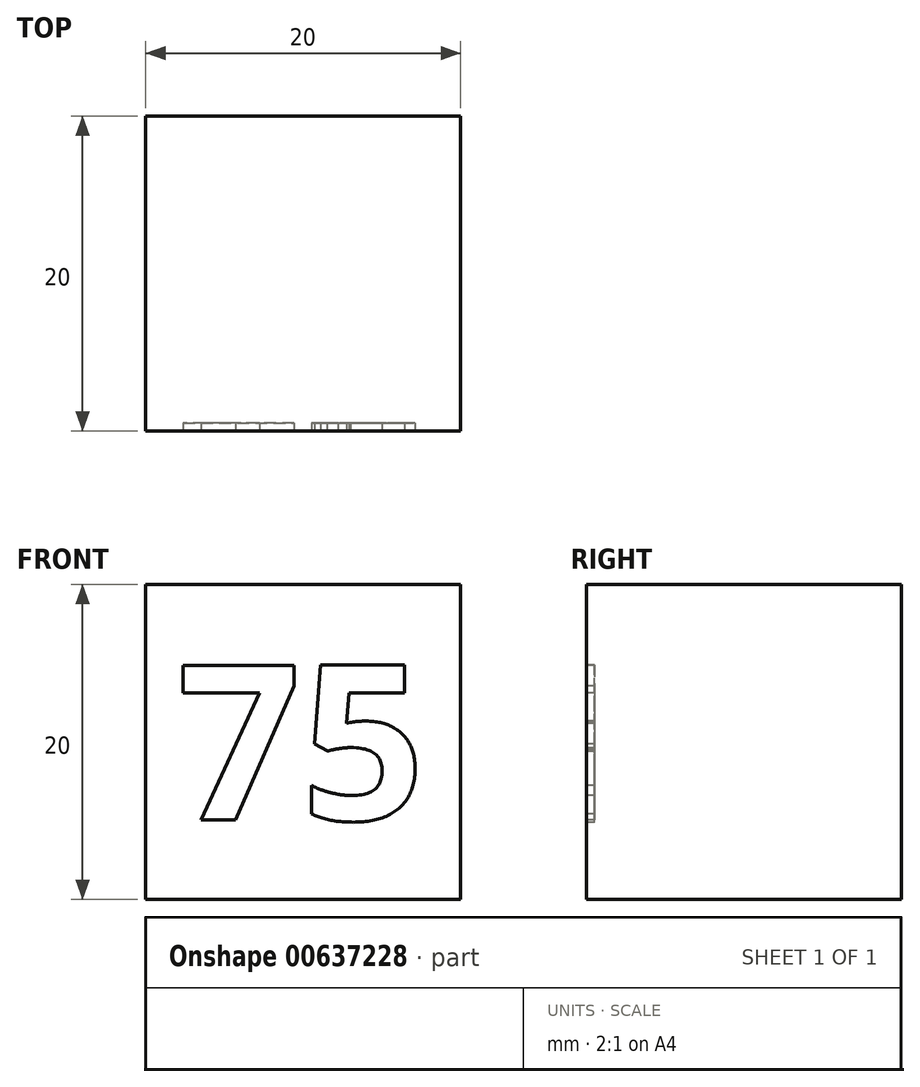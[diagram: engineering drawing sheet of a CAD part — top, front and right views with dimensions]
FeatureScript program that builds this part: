
annotation { "Feature Type Name" : "Feature", "Feature Type Description" : "" }
export const myFeature = defineFeature(function(context is Context, id is Id, definition is map)
    precondition{}
    {
        {
            var Q0;
            Q0=qCreatedBy(makeId("Top.planeOp"),FACE);
            var sketch = newSketch(context, id + "F0", { "sketchPlane" : qUnion([Q0])});
            skLineSegment(sketch, "E0.bottom", {"start": v(10, -10) * mm, "end": v(-10, -10) * mm});
            skLineSegment(sketch, "E0.top", {"start": v(10, 10) * mm, "end": v(-10, 10) * mm});
            skLineSegment(sketch, "E0.left", {"start": v(10, -10) * mm, "end": v(10, 10) * mm});
            skLineSegment(sketch, "E0.right", {"start": v(-10, -10) * mm, "end": v(-10, 10) * mm});
            skPoint(sketch, "E0.middle", {"position": v(0, 0) * mm});
            skSolve(sketch);
        }
        {
            var Q0;
            Q0 = qSketchRegion(id + "F0", true);
            extrude(context, id + "F1", {"entities" : qUnion([Q0]), "endBound" : BoundingType.SYMMETRIC, "depth" : 20 * mm, "offsetDistance" : 25 * mm});
        }
        {
            var Q0;
            Q0=makeQuery(id+"F1.opExtrude","SWEPT_FACE",FACE,{"disambiguationData":[OSD([sQuery(id+"F0.wireOp",EDGE,"E0.bottom")])]});
            var sketch = newSketch(context, id + "F2", { "sketchPlane" : qUnion([Q0])});
            skText(sketch, "E1", { "text": "75", "fontName": "OpenSans-Bold.ttf"});
            skLineSegment(sketch, "E2", {"start": v(-8, 0) * mm, "end": v(8, 0) * mm, "construction": true});
            const initialGuessF2  = {"E1": [-0.008, -0.00496, 1, 0, 0.00992]};
            skSetInitialGuess(sketch, initialGuessF2);
            skSolve(sketch);
        }
        {
            var Q0;
            Q0 = qSketchRegion(id + "F2", true);
            extrude(context, id + "F3", {"entities" : qUnion([Q0]), "operationType" : NewBodyOperationType.REMOVE, "oppositeDirection" : true, "depth" : 0.5 * mm, "offsetDistance" : 25 * mm});
        }
    });
